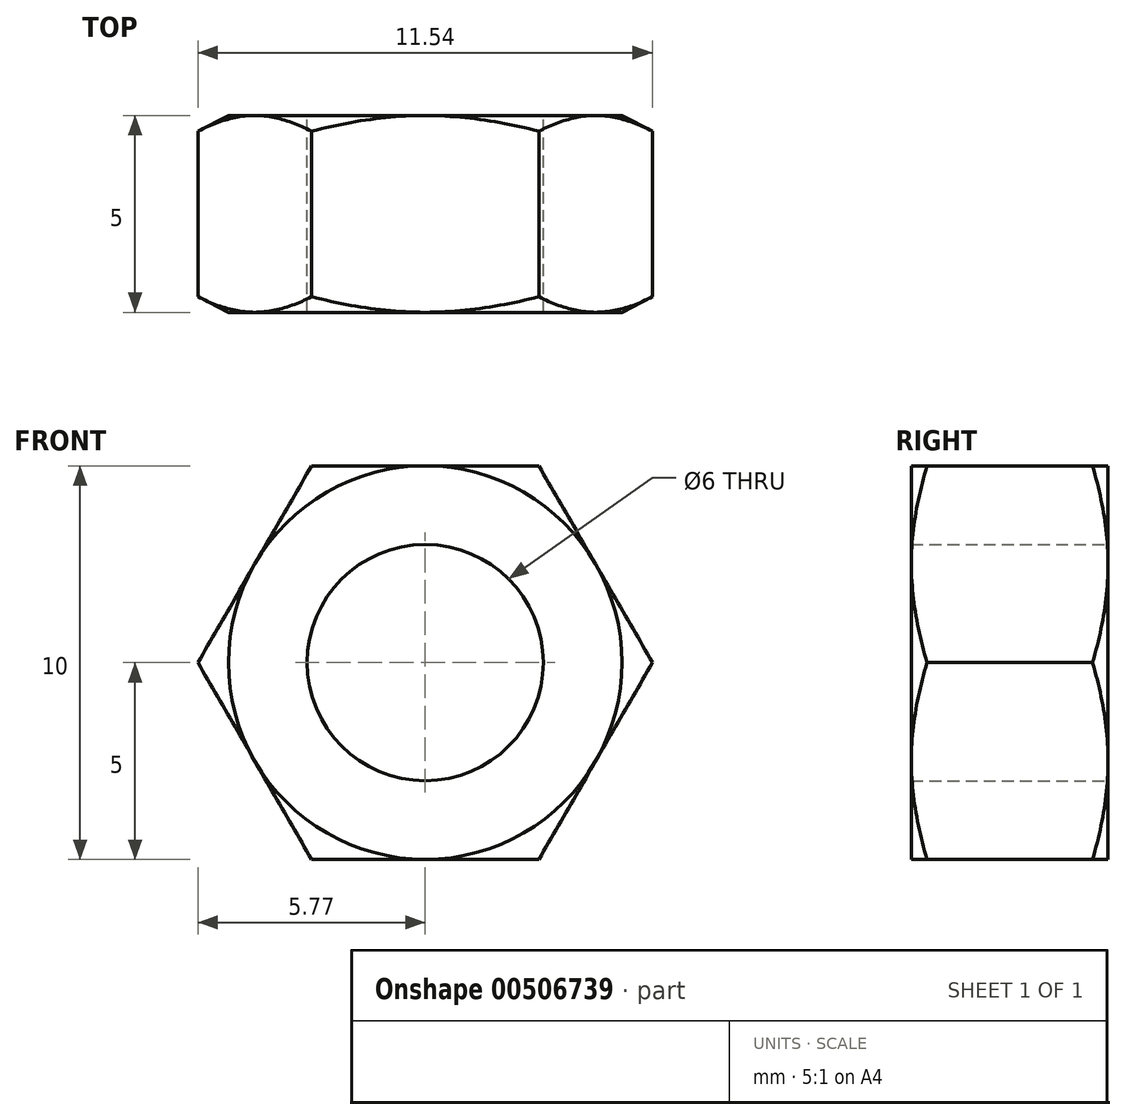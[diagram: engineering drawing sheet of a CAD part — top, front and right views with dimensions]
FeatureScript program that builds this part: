
annotation { "Feature Type Name" : "Feature", "Feature Type Description" : "" }
export const myFeature = defineFeature(function(context is Context, id is Id, definition is map)
    precondition{}
    {
        {
            var Q0;
            Q0=qCreatedBy(makeId("Front.planeOp"),FACE);
            var sketch = newSketch(context, id + "F0", { "sketchPlane" : qUnion([Q0])});
            skCircle(sketch, "E0", {"center": v(0, 0) * mm, "radius": 3 * mm});
            skCircle(sketch, "E1.cCircle", {"center": v(0, 0) * mm, "radius": 5 * mm, "construction": true});
            skLineSegment(sketch, "E1.0", {"start": v(2.89, -5) * mm, "end": v(-2.89, -5) * mm});
            skLineSegment(sketch, "E1.1", {"start": v(-2.89, -5) * mm, "end": v(-5.77, 0) * mm});
            skLineSegment(sketch, "E1.2", {"start": v(-5.77, 0) * mm, "end": v(-2.89, 5) * mm});
            skLineSegment(sketch, "E1.3", {"start": v(-2.89, 5) * mm, "end": v(2.89, 5) * mm});
            skLineSegment(sketch, "E1.4", {"start": v(2.89, 5) * mm, "end": v(5.77, 0) * mm});
            skLineSegment(sketch, "E1.5", {"start": v(5.77, 0) * mm, "end": v(2.89, -5) * mm});
            skPoint(sketch, "E1.0.midPoint", {"position": v(0, -5) * mm});
            skSolve(sketch);
        }
        {
            var Q0;
            Q0 = qSketchRegion(id + "F0", true);
            extrude(context, id + "F1", {"entities" : qUnion([Q0]), "depth" : 5 * mm, "offsetDistance" : 25 * mm});
        }
        {
            var Q0;
            Q0=qCreatedBy(makeId("Top.planeOp"),FACE);
            var sketch = newSketch(context, id + "F2", { "sketchPlane" : qUnion([Q0])});
            skLineSegment(sketch, "E2", {"start": v(0, 0) * mm, "end": v(-5, 0) * mm});
            skLineSegment(sketch, "E3", {"start": v(-5, 0) * mm, "end": v(-5.78, -0.4) * mm});
            skLineSegment(sketch, "E4", {"start": v(0, -5) * mm, "end": v(-5, -5) * mm});
            skLineSegment(sketch, "E5", {"start": v(-5, -5) * mm, "end": v(-5.78, -4.6) * mm});
            skLineSegment(sketch, "E6", {"start": v(-5.78, -4.6) * mm, "end": v(-5.94, -5.67) * mm});
            skLineSegment(sketch, "E7", {"start": v(-5.94, -5.67) * mm, "end": v(0, -5.67) * mm});
            skLineSegment(sketch, "E8", {"start": v(0, -5.67) * mm, "end": v(0, -5) * mm});
            skLineSegment(sketch, "E9", {"start": v(-5.78, -0.4) * mm, "end": v(-6.07, 0.44) * mm});
            skLineSegment(sketch, "E10", {"start": v(-6.07, 0.44) * mm, "end": v(0, 0.44) * mm});
            skLineSegment(sketch, "E11", {"start": v(0, 0.44) * mm, "end": v(0, 0) * mm});
            skSolve(sketch);
        }
        {
            var Q0;
            Q0 = qSketchRegion(id + "F2", true);
            var Q1;
            Q1=sQuery(id+"F2.wireOp",EDGE,"E11");
            revolve(context, id + "F3", {"operationType" : NewBodyOperationType.REMOVE, "entities" : qUnion([Q0]), "axis" : qUnion([Q1]), "revolveType" : RevolveType.FULL, "oppositeDirection" : true});
        }
    });
